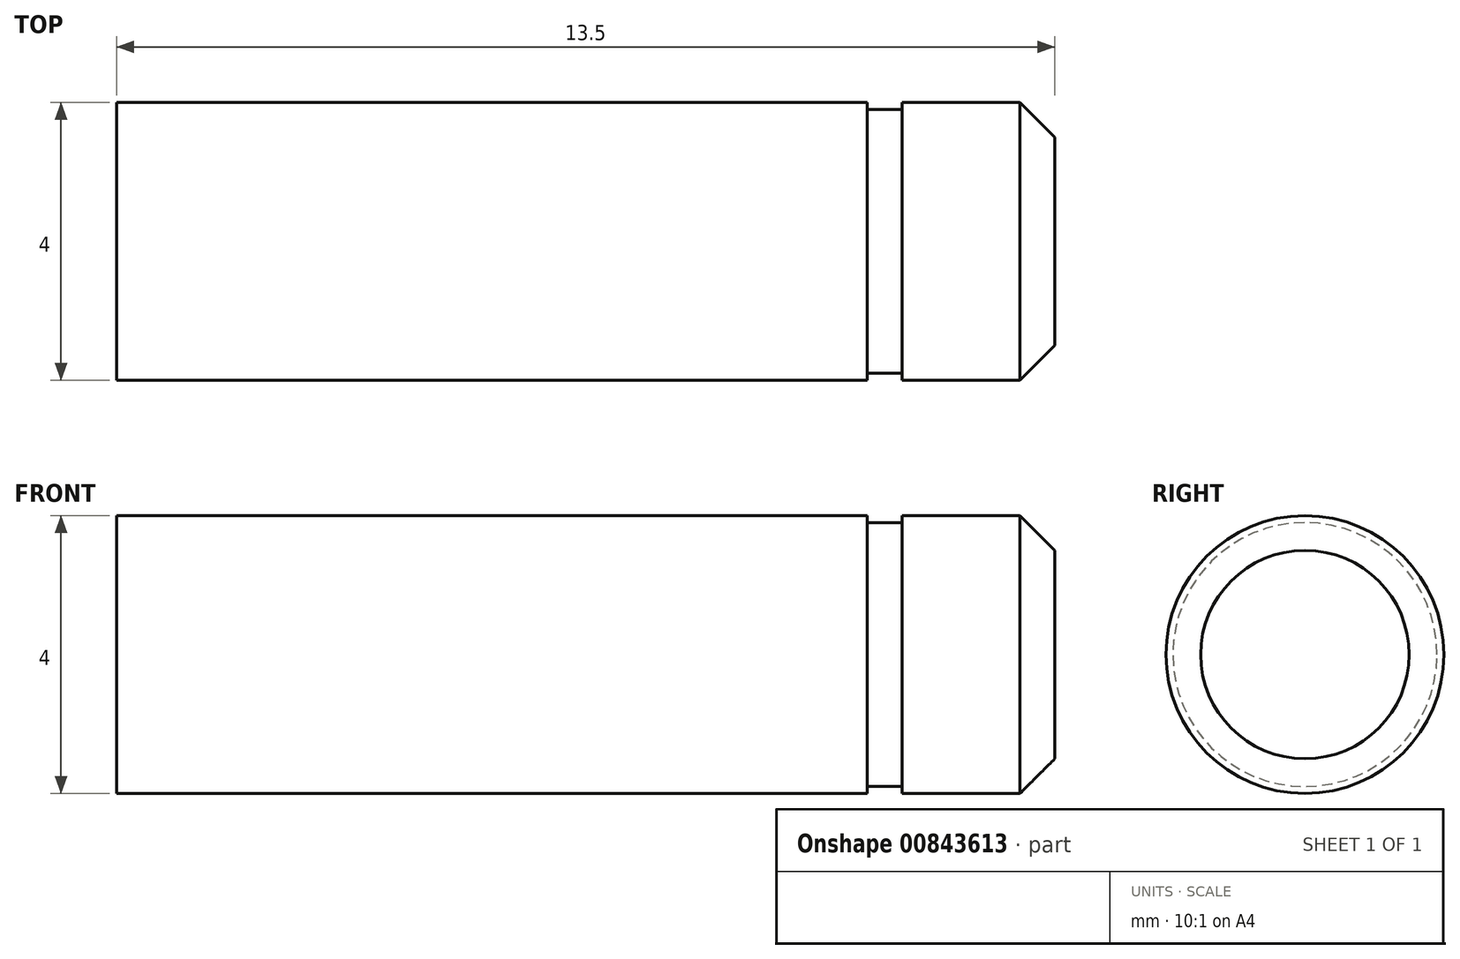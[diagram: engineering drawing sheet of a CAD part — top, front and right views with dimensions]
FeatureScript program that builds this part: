
annotation { "Feature Type Name" : "Feature", "Feature Type Description" : "" }
export const myFeature = defineFeature(function(context is Context, id is Id, definition is map)
    precondition{}
    {
        {
            var Q0;
            Q0=qCreatedBy(makeId("Right.planeOp"),FACE);
            var sketch = newSketch(context, id + "F0", { "sketchPlane" : qUnion([Q0])});
            skCircle(sketch, "E0", {"center": v(0, 0) * mm, "radius": 2 * mm});
            skSolve(sketch);
        }
        {
            var Q0;
            Q0 = qSketchRegion(id + "F0", true);
            extrude(context, id + "F1", {"entities" : qUnion([Q0]), "oppositeDirection" : true, "depth" : 2.2 * mm, "offsetDistance" : 25 * mm});
        }
        {
            var Q0;
            Q0=makeQuery(id+"F1.opExtrude","CAP_FACE",FACE,{"disambiguationData":[OSD([sQuery(id+"F0.wireOp",EDGE,"E0")])],"isStart":false});
            var sketch = newSketch(context, id + "F2", { "sketchPlane" : qUnion([Q0])});
            skCircle(sketch, "E1", {"center": v(0, 0) * mm, "radius": 1.9 * mm});
            skSolve(sketch);
        }
        {
            var Q0;
            Q0=makeQuery(id+"F2.imprint","IMPRINT",FACE,{"disambiguationData":[TD([[makeQuery(id+"F2.imprint","IMPRINT",EDGE,{"derivedFrom":sQuery(id+"F2.wireOp",EDGE,"E1")}),1.0]])]});
            extrude(context, id + "F3", {"entities" : qUnion([Q0]), "operationType" : NewBodyOperationType.ADD, "depth" : .5 * mm, "offsetDistance" : 25 * mm});
        }
        {
            var Q0;
            Q0=makeQuery(id+"F3.opExtrude","CAP_FACE",FACE,{"disambiguationData":[OSD([sQuery(id+"F2.wireOp",EDGE,"E1")])],"isStart":false});
            var sketch = newSketch(context, id + "F4", { "sketchPlane" : qUnion([Q0])});
            skCircle(sketch, "E2", {"center": v(0, 0) * mm, "radius": 2 * mm});
            skSolve(sketch);
        }
        {
            var Q0;
            Q0 = qSketchRegion(id + "F4", true);
            extrude(context, id + "F5", {"entities" : qUnion([Q0]), "operationType" : NewBodyOperationType.ADD, "depth" : 10.8 * mm, "offsetDistance" : 25 * mm});
        }
        {
            var Q0;
            Q0=makeQuery(id+"F1.opExtrude","CAP_EDGE",EDGE,{"disambiguationData":[OSD([sQuery(id+"F0.wireOp",EDGE,"E0")])],"isStart":true});
            chamfer(context, id + "F6", {"entities" : qUnion([Q0]), "width" : .5 * mm, "tangentPropagation" : true});
        }
    });
